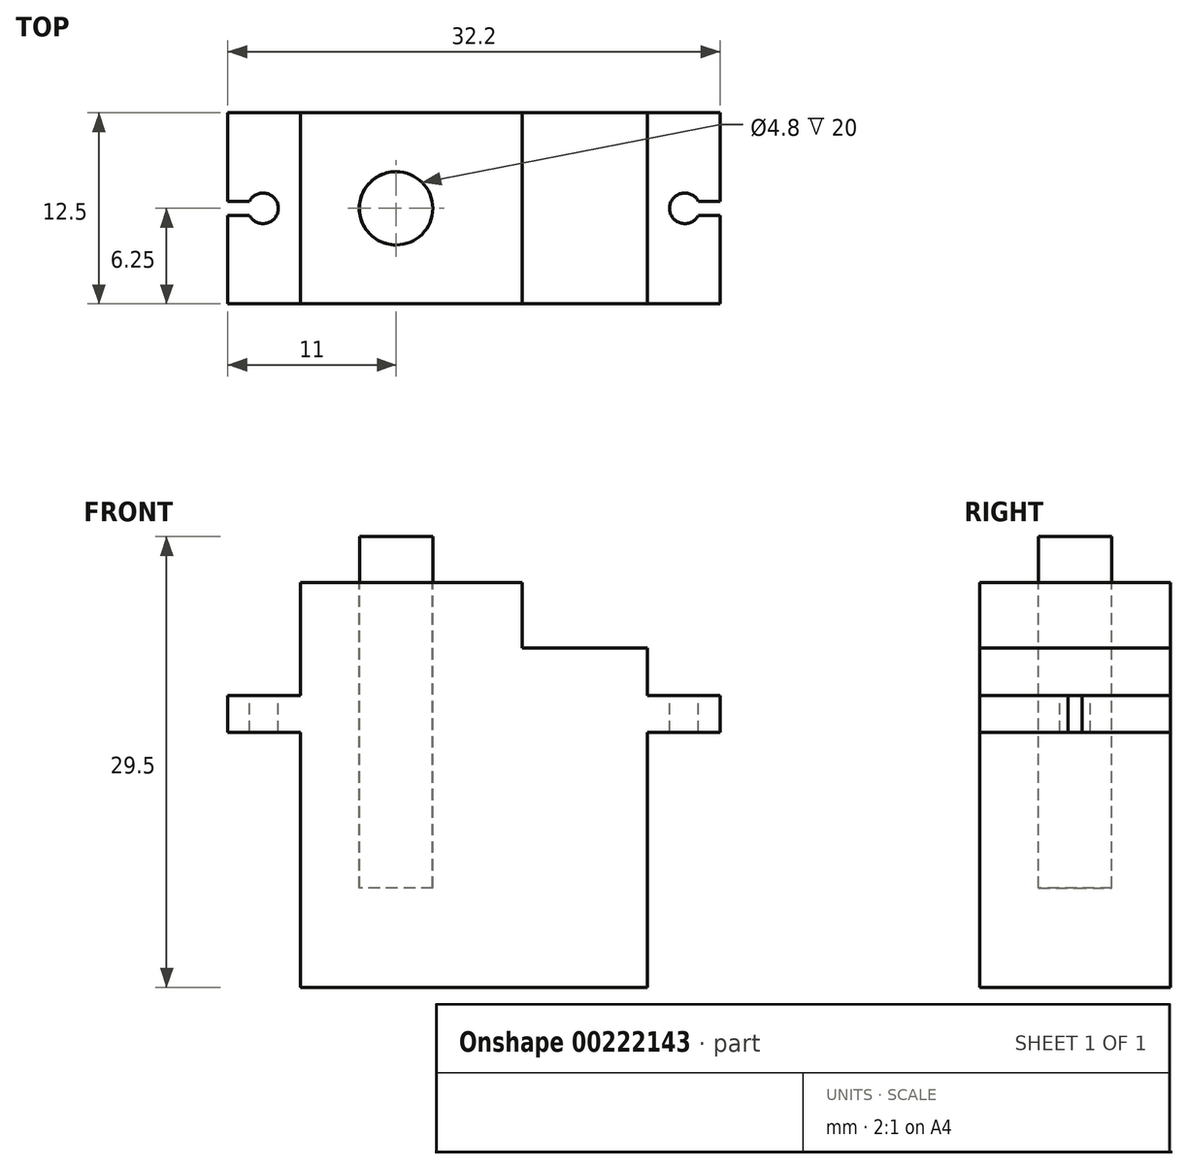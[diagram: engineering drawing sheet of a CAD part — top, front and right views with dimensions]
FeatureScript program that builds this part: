
annotation { "Feature Type Name" : "Feature", "Feature Type Description" : "" }
export const myFeature = defineFeature(function(context is Context, id is Id, definition is map)
    precondition{}
    {
        {
            var Q0;
            Q0=qCreatedBy(makeId("Top.planeOp"),FACE);
            var sketch = newSketch(context, id + "F0", { "sketchPlane" : qUnion([Q0])});
            skLineSegment(sketch, "E0.bottom", {"start": v(11.35, 6.25) * mm, "end": v(-11.35, 6.25) * mm});
            skLineSegment(sketch, "E0.top", {"start": v(11.35, -6.25) * mm, "end": v(-11.35, -6.25) * mm});
            skLineSegment(sketch, "E0.left", {"start": v(11.35, 6.25) * mm, "end": v(11.35, -6.25) * mm});
            skLineSegment(sketch, "E0.right", {"start": v(-11.35, 6.25) * mm, "end": v(-11.35, -6.25) * mm});
            skPoint(sketch, "E0.middle", {"position": v(0, 0) * mm});
            skSolve(sketch);
        }
        {
            var Q0;
            Q0 = qSketchRegion(id + "F0", true);
            extrude(context, id + "F1", {"entities" : qUnion([Q0]), "depth" : 16.7 * mm});
        }
        {
            var Q0;
            Q0=makeQuery(id+"F1.opExtrude","CAP_FACE",FACE,{"disambiguationData":[OSD([sQuery(id+"F0.wireOp",EDGE,"E0.bottom"),sQuery(id+"F0.wireOp",EDGE,"E0.top"),sQuery(id+"F0.wireOp",EDGE,"E0.left"),sQuery(id+"F0.wireOp",EDGE,"E0.right")])],"isStart":false});
            var sketch = newSketch(context, id + "F2", { "sketchPlane" : qUnion([Q0])});
            skLineSegment(sketch, "E1.bottom", {"start": v(16.1, -6.25) * mm, "end": v(-16.1, -6.25) * mm});
            skLineSegment(sketch, "E1.top", {"start": v(16.1, 6.25) * mm, "end": v(-16.1, 6.25) * mm});
            skLineSegment(sketch, "E1.left", {"start": v(16.1, -6.25) * mm, "end": v(16.1, 6.25) * mm});
            skLineSegment(sketch, "E1.right", {"start": v(-16.1, -6.25) * mm, "end": v(-16.1, 6.25) * mm});
            skPoint(sketch, "E1.middle", {"position": v(0, 0) * mm});
            skSolve(sketch);
        }
        {
            var Q0;
            Q0 = qSketchRegion(id + "F2", true);
            extrude(context, id + "F3", {"entities" : qUnion([Q0]), "operationType" : NewBodyOperationType.ADD, "depth" : 2.4 * mm});
        }
        {
            var Q0;
            Q0=makeQuery(id+"F3.opExtrude","CAP_FACE",FACE,{"disambiguationData":[OSD([sQuery(id+"F2.wireOp",EDGE,"E1.bottom"),sQuery(id+"F2.wireOp",EDGE,"E1.top"),sQuery(id+"F2.wireOp",EDGE,"E1.left"),sQuery(id+"F2.wireOp",EDGE,"E1.right")])],"isStart":false});
            var sketch = newSketch(context, id + "F4", { "sketchPlane" : qUnion([Q0])});
            skLineSegment(sketch, "E2", {"start": v(-16.1, 0) * mm, "end": v(16.1, 0) * mm, "construction": true});
            skCircle(sketch, "E3", {"center": v(0, 0) * mm, "radius": 13.8 * mm, "construction": true});
            skCircle(sketch, "E4", {"center": v(-13.8, 0) * mm, "radius": 1 * mm});
            skLineSegment(sketch, "E5.bottom", {"start": v(-16.1, 0.46) * mm, "end": v(-13.5, 0.46) * mm});
            skLineSegment(sketch, "E5.top", {"start": v(-16.1, -0.46) * mm, "end": v(-13.5, -0.46) * mm});
            skLineSegment(sketch, "E5.left", {"start": v(-16.1, 0.46) * mm, "end": v(-16.1, -0.46) * mm});
            skLineSegment(sketch, "E5.right", {"start": v(-13.5, 0.46) * mm, "end": v(-13.5, -0.46) * mm});
            skPoint(sketch, "E5.middle", {"position": v(-14.8, 0) * mm});
            skLineSegment(sketch, "E6.MirrorCS", {"start": v(13.5, 0.46) * mm, "end": v(13.5, -0.46) * mm});
            skLineSegment(sketch, "E7.MirrorCS", {"start": v(16.1, 0.46) * mm, "end": v(16.1, -0.46) * mm});
            skLineSegment(sketch, "E8.MirrorCS", {"start": v(16.1, 0.46) * mm, "end": v(13.5, 0.46) * mm});
            skLineSegment(sketch, "E9.MirrorCS", {"start": v(16.1, -0.46) * mm, "end": v(13.5, -0.46) * mm});
            skCircle(sketch, "E10.MirrorC", {"center": v(13.8, 0) * mm, "radius": 1 * mm});
            skPoint(sketch, "E11.MirrorP", {"position": v(14.8, 0) * mm});
            skSolve(sketch);
        }
        {
            var Q0;
            Q0 = qSketchRegion(id + "F4", true);
            extrude(context, id + "F5", {"entities" : qUnion([Q0]), "operationType" : NewBodyOperationType.REMOVE, "endBound" : BoundingType.THROUGH_ALL, "oppositeDirection" : true, "depth" : 25 * mm});
        }
        {
            var Q0;
            Q0=makeQuery(id+"F1.opExtrude","CAP_FACE",FACE,{"disambiguationData":[OSD([sQuery(id+"F0.wireOp",EDGE,"E0.bottom"),sQuery(id+"F0.wireOp",EDGE,"E0.top"),sQuery(id+"F0.wireOp",EDGE,"E0.left"),sQuery(id+"F0.wireOp",EDGE,"E0.right")])],"isStart":true});
            extrude(context, id + "F6", {"entities" : qUnion([Q0]), "operationType" : NewBodyOperationType.ADD, "oppositeDirection" : true, "depth" : 22.2 * mm});
        }
        {
            var Q0;
            Q0=makeQuery(id+"F6.opExtrude","CAP_FACE",FACE,{"disambiguationData":[OSD([sQuery(id+"F0.wireOp",EDGE,"E0.bottom"),sQuery(id+"F0.wireOp",EDGE,"E0.top"),sQuery(id+"F0.wireOp",EDGE,"E0.left"),sQuery(id+"F0.wireOp",EDGE,"E0.right")])],"isStart":false});
            var sketch = newSketch(context, id + "F7", { "sketchPlane" : qUnion([Q0])});
            skLineSegment(sketch, "E12.bottom", {"start": v(-11.35, 6.25) * mm, "end": v(3.15, 6.25) * mm});
            skLineSegment(sketch, "E12.top", {"start": v(-11.35, -6.25) * mm, "end": v(3.15, -6.25) * mm});
            skLineSegment(sketch, "E12.left", {"start": v(-11.35, 6.25) * mm, "end": v(-11.35, -6.25) * mm});
            skLineSegment(sketch, "E12.right", {"start": v(3.15, 6.25) * mm, "end": v(3.15, -6.25) * mm});
            skSolve(sketch);
        }
        {
            var Q0;
            Q0 = qSketchRegion(id + "F7", true);
            extrude(context, id + "F8", {"entities" : qUnion([Q0]), "operationType" : NewBodyOperationType.ADD, "depth" : 4.3 * mm});
        }
        {
            var Q0;
            Q0=makeQuery(id+"F8.opExtrude","CAP_FACE",FACE,{"disambiguationData":[OSD([sQuery(id+"F7.wireOp",EDGE,"E12.bottom"),sQuery(id+"F7.wireOp",EDGE,"E12.top"),sQuery(id+"F7.wireOp",EDGE,"E12.left"),sQuery(id+"F7.wireOp",EDGE,"E12.right")])],"isStart":false});
            var sketch = newSketch(context, id + "F9", { "sketchPlane" : qUnion([Q0])});
            skCircle(sketch, "E13", {"center": v(-11.35, 0) * mm, "radius": 6.25 * mm, "construction": true});
            skCircle(sketch, "E14", {"center": v(-5.1, 0) * mm, "radius": 2.4 * mm});
            skSolve(sketch);
        }
        {
            var Q0;
            Q0=makeQuery(id+"F1.opExtrude","SWEPT_BODY",BODY,{"disambiguationData":[OSD([sQuery(id+"F0.wireOp",EDGE,"E0.bottom"),sQuery(id+"F0.wireOp",EDGE,"E0.top"),sQuery(id+"F0.wireOp",EDGE,"E0.left"),sQuery(id+"F0.wireOp",EDGE,"E0.right")])]});
            transform(context, id + "F10", {"entities" : qUnion([Q0]), "transformType" : TransformType.TRANSLATION_3D, "dx" : 0 * mm, "dy" : 0 * mm, "dz" : 0 * mm, "makeCopy" : true});
        }
        {
            var Q0;
            Q0=makeQuery(id+"F10.opPattern","COPY",BODY,{"derivedFrom":makeQuery(id+"F1.opExtrude","SWEPT_BODY",BODY,{"disambiguationData":[OSD([sQuery(id+"F0.wireOp",EDGE,"E0.bottom"),sQuery(id+"F0.wireOp",EDGE,"E0.top"),sQuery(id+"F0.wireOp",EDGE,"E0.left"),sQuery(id+"F0.wireOp",EDGE,"E0.right")])]}),"instanceName":"1"});
            deleteBodies(context, id + "F11", {"entities" : qUnion([Q0])});
        }
        {
            var Q0;
            Q0=makeQuery(id+"F8.opExtrude","CAP_FACE",FACE,{"disambiguationData":[OSD([sQuery(id+"F7.wireOp",EDGE,"E12.bottom"),sQuery(id+"F7.wireOp",EDGE,"E12.top"),sQuery(id+"F7.wireOp",EDGE,"E12.left"),sQuery(id+"F7.wireOp",EDGE,"E12.right")])],"isStart":false});
            var sketch = newSketch(context, id + "F12", { "sketchPlane" : qUnion([Q0])});
            skCircle(sketch, "E15", {"center": v(-5.1, 0) * mm, "radius": 2.4 * mm});
            skSolve(sketch);
        }
        {
            var Q0;
            Q0 = qSketchRegion(id + "F12", true);
            extrude(context, id + "F13", {"entities" : qUnion([Q0]), "operationType" : NewBodyOperationType.REMOVE, "oppositeDirection" : true, "depth" : 20 * mm});
        }
        {
            var Q0;
            Q0=makeQuery(id+"F9.imprint","IMPRINT",FACE,{"disambiguationData":[TD([[makeQuery(id+"F9.imprint","IMPRINT",EDGE,{"derivedFrom":sQuery(id+"F9.wireOp",EDGE,"E14")}),-1.0]])]});
            var sketch = newSketch(context, id + "F14", { "sketchPlane" : qUnion([Q0])});
            skCircle(sketch, "E16", {"center": v(-5.1, 0) * mm, "radius": 2.4 * mm});
            skSolve(sketch);
        }
        {
            var Q0;
            Q0 = qSketchRegion(id + "F14", true);
            extrude(context, id + "F15", {"entities" : qUnion([Q0]), "depth" : 3 * mm});
        }
        {
            var Q0;
            Q0=makeQuery(id+"F15.opExtrude","CAP_FACE",FACE,{"disambiguationData":[OSD([sQuery(id+"F14.wireOp",EDGE,"E16")])],"isStart":false});
            extrude(context, id + "F16", {"entities" : qUnion([Q0]), "oppositeDirection" : true, "depth" : 23 * mm});
        }
        {
            var Q0;
            Q0=makeQuery(id+"F15.opExtrude","SWEPT_BODY",BODY,{"disambiguationData":[OSD([sQuery(id+"F14.wireOp",EDGE,"E16")])]});
            deleteBodies(context, id + "F17", {"entities" : qUnion([Q0])});
        }
    });
